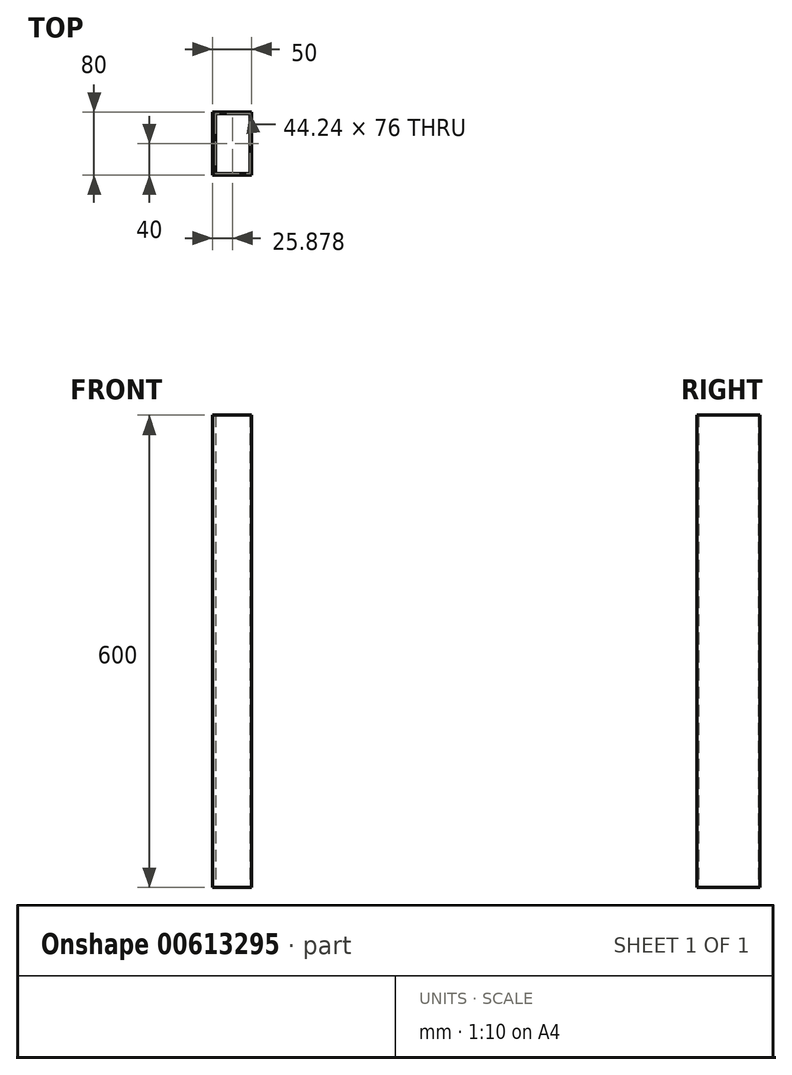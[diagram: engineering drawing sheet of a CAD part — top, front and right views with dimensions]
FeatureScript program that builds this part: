
annotation { "Feature Type Name" : "Feature", "Feature Type Description" : "" }
export const myFeature = defineFeature(function(context is Context, id is Id, definition is map)
    precondition{}
    {
        {
            var Q0;
            Q0=qCreatedBy(makeId("Top.planeOp"),FACE);
            var sketch = newSketch(context, id + "F0", { "sketchPlane" : qUnion([Q0])});
            skLineSegment(sketch, "E0.bottom", {"start": v(-25, 40) * mm, "end": v(25, 40) * mm});
            skLineSegment(sketch, "E0.top", {"start": v(-25, -40) * mm, "end": v(25, -40) * mm});
            skLineSegment(sketch, "E0.left", {"start": v(-25, 40) * mm, "end": v(-25, -40) * mm});
            skLineSegment(sketch, "E0.right", {"start": v(25, 40) * mm, "end": v(25, -40) * mm});
            skLineSegment(sketch, "E1.bottom", {"start": v(-21.24, 38) * mm, "end": v(23, 38) * mm});
            skLineSegment(sketch, "E1.top", {"start": v(-21.24, -38) * mm, "end": v(23, -38) * mm});
            skLineSegment(sketch, "E1.left", {"start": v(-21.24, 38) * mm, "end": v(-21.24, -38) * mm});
            skLineSegment(sketch, "E1.right", {"start": v(23, 38) * mm, "end": v(23, -38) * mm});
            skSolve(sketch);
        }
        {
            var Q0;
            Q0 = qSketchRegion(id + "F0", true);
            extrude(context, id + "F1", {"entities" : qUnion([Q0]), "depth" : 600 * mm, "offsetDistance" : 25 * mm});
        }
    });
